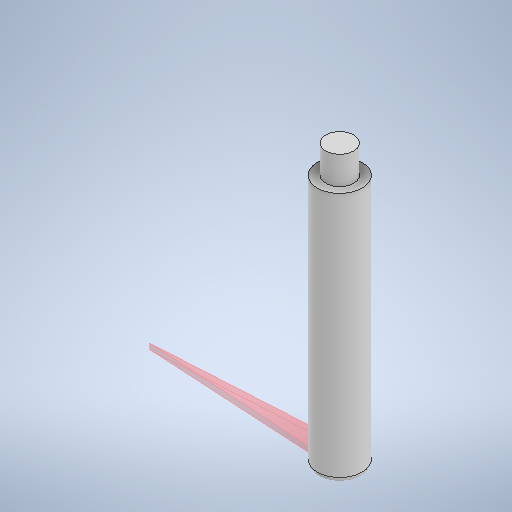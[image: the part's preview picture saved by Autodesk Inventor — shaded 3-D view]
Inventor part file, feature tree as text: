
AUTODESK INVENTOR PART (.ipt)
format: ipt  version: 2025.1 (Build 291241000, 241)  size: 273,920 bytes
history: native  units: mm
features: extrude x4, sketch x2, plane x1, fillet x1, other x1
ambient origin geometry x8: Origin, YZ Plane, XZ Plane, XY Plane, X Axis, Y Axis, Z Axis, Center Point
bodies: Solid3 (feature_tree)
feature tree (9):
  sketch  "Sketch1"  dims[d0=8.0mm d7=-43.0mm]
  extrude  "Extrusion4"  [1 undecoded]
  extrude  "Extrusion5"  Depth=1.0mm
  extrude  "Extrusion6"  Depth=1.0mm TaperAngle=0.0deg
  plane  "Work Plane1"
  extrude  "Extrusion3"  Depth=1.0mm TaperAngle=0.0deg
  fillet  "Fillet2"  Radius=45.0mm
  sketch  "Sketch2"  dims[d9=30.0mm d10=3.5mm d11=1.0mm d12=0.0mm d13=40.0mm d14=0.0mm d15=45.0mm d16=0.0mm d17=5.0mm d18=0.0mm d19=5.0mm d20=1.0mm]
  other  "Needle"
note: 1 required parameter value undecoded (feature->parameter linkage not recoverable at this tier; creation-order binding heuristic only, values carry confidence <= 0.55)
